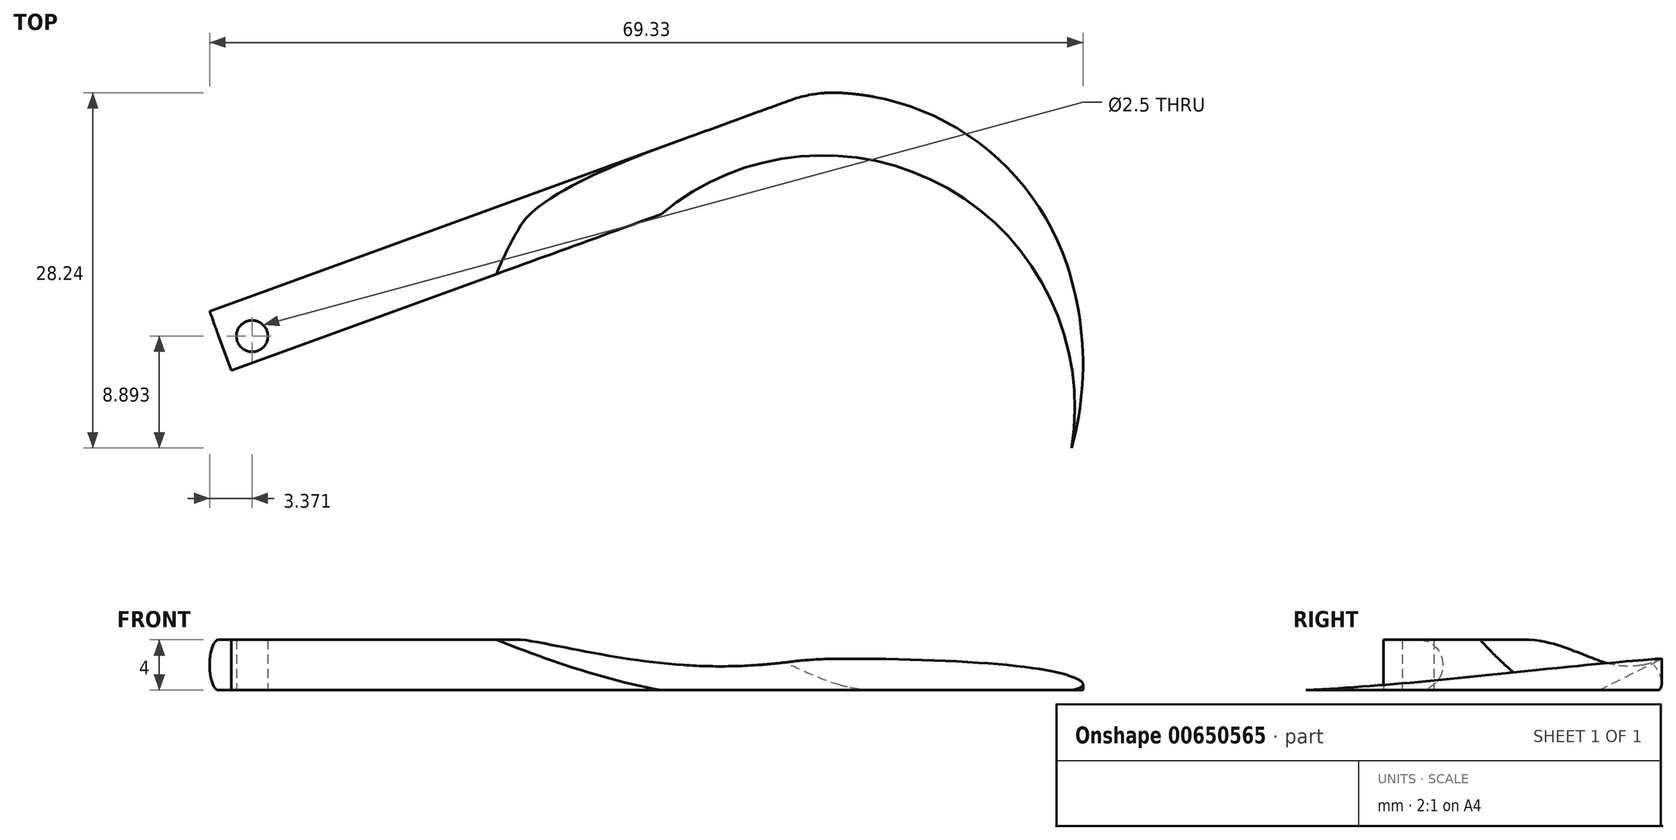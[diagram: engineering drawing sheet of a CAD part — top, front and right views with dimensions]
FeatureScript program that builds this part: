
annotation { "Feature Type Name" : "Feature", "Feature Type Description" : "" }
export const myFeature = defineFeature(function(context is Context, id is Id, definition is map)
    precondition{}
    {
        {
            var Q0;
            Q0=qCreatedBy(makeId("Top.planeOp"),FACE);
            var sketch = newSketch(context, id + "F0", { "sketchPlane" : qUnion([Q0])});
            skArc(sketch, "E0", {"start": v(19.73, -3.26) * mm, "mid": v(15.25, 12.94) * mm, "end": v(0, 20) * mm});
            skArc(sketch, "E1", {"start": v(13.13, 21.27) * mm, "mid": v(6.38, 24.17) * mm, "end": v(-0.93, 24.98) * mm});
            skArc(sketch, "E2", {"start": v(13.13, 21.27) * mm, "mid": v(19.78, 9.9) * mm, "end": v(19.73, -3.26) * mm});
            skPoint(sketch, "E3", {"position": v(19.73, -3.26) * mm});
            skPoint(sketch, "E4", {"position": v(13.13, 21.27) * mm});
            skPoint(sketch, "E5", {"position": v(0, 25) * mm});
            skPoint(sketch, "E6", {"position": v(0, 20) * mm});
            skLineSegment(sketch, "E7.bottom", {"start": v(0, 20) * mm, "end": v(-46.98, 2.9) * mm});
            skLineSegment(sketch, "E7.top", {"start": v(-1.71, 24.7) * mm, "end": v(-48.7, 7.6) * mm});
            skLineSegment(sketch, "E7.left", {"start": v(0, 20) * mm, "end": v(-1.71, 24.7) * mm});
            skLineSegment(sketch, "E7.right", {"start": v(-46.98, 2.9) * mm, "end": v(-48.7, 7.6) * mm});
            skLineSegment(sketch, "E8", {"start": v(-5.23, 23.42) * mm, "end": v(-0.93, 24.98) * mm});
            skCircle(sketch, "E9", {"center": v(-45.32, 5.63) * mm, "radius": 1.25 * mm});
            skSolve(sketch);
        }
        {
            var Q0;
            Q0=makeQuery(id+"F0.imprint","IMPRINT",FACE,{"disambiguationData":[TD([[makeQuery(id+"F0.imprint","IMPRINT",EDGE,{"derivedFrom":sQuery(id+"F0.wireOp",EDGE,"E7.bottom")}),-1.0]])]});
            var Q1;
            Q1=makeQuery(id+"F0.imprint","IMPRINT",FACE,{"disambiguationData":[TD([[makeQuery(id+"F0.imprint","IMPRINT",EDGE,{"derivedFrom":sQuery(id+"F0.wireOp",EDGE,"E0")}),-1.0]])]});
            extrude(context, id + "F1", {"entities" : qUnion([Q0, Q1]), "depth" : 4 * mm, "offsetDistance" : 25 * mm});
        }
        {
            var Q0;
            Q0=makeQuery(id+"F1.opExtrude","SWEPT_EDGE",EDGE,{"disambiguationData":[OSD([sQuery(id+"F0.wireOp",EDGE,"E0"),sQuery(id+"F0.wireOp",EDGE,"E7.bottom"),sQuery(id+"F0.wireOp",EDGE,"E7.left")])]});
            fillet(context, id + "F2", {"entities" : qUnion([Q0]), "radius" : 10 * mm, "tangentPropagation" : true, "allowEdgeOverflow" : false});
        }
        {
            var Q0;
            Q0=makeQuery(id+"F1.opExtrude","CAP_EDGE",EDGE,{"disambiguationData":[OSD([sQuery(id+"F0.wireOp",EDGE,"E0")])],"isStart":false});
            chamfer(context, id + "F3", {"entities" : qUnion([Q0]), "chamferType" : ChamferType.TWO_OFFSETS, "width1" : 4 * mm, "oppositeDirection" : false, "width2" : 8 * mm});
        }
        {
            var Q0;
            Q0=makeQuery(id+"F1.opExtrude","SWEPT_EDGE",EDGE,{"disambiguationData":[OSD([sQuery(id+"F0.wireOp",EDGE,"E1"),sQuery(id+"F0.wireOp",EDGE,"E2")])]});
            fillet(context, id + "F4", {"entities" : qUnion([Q0]), "radius" : 20 * mm, "tangentPropagation" : true, "allowEdgeOverflow" : false});
        }
        {
            var Q0;
            Q0=makeQuery(id+"F1.opExtrude","SWEPT_EDGE",EDGE,{"disambiguationData":[OSD([sQuery(id+"F0.wireOp",EDGE,"E1"),sQuery(id+"F0.wireOp",EDGE,"E8")])]});
            fillet(context, id + "F5", {"entities" : qUnion([Q0]), "radius" : 10 * mm, "tangentPropagation" : true, "allowEdgeOverflow" : false});
        }
        {
            var Q0;
            Q0=makeQuery(id+"F1.opExtrude","CAP_EDGE",EDGE,{"disambiguationData":[OSD([sQuery(id+"F0.wireOp",EDGE,"E7.top"),sQuery(id+"F0.wireOp",EDGE,"E8")])],"isStart":false});
            var Q1;
            Q1=makeQuery(id+"F1.opExtrude","CAP_EDGE",EDGE,{"disambiguationData":[OSD([sQuery(id+"F0.wireOp",EDGE,"E7.top"),sQuery(id+"F0.wireOp",EDGE,"E8")])],"isStart":true});
            fillet(context, id + "F6", {"entities" : qUnion([Q0, Q1]), "radius" : 2 * mm, "allowEdgeOverflow" : false});
        }
    });
